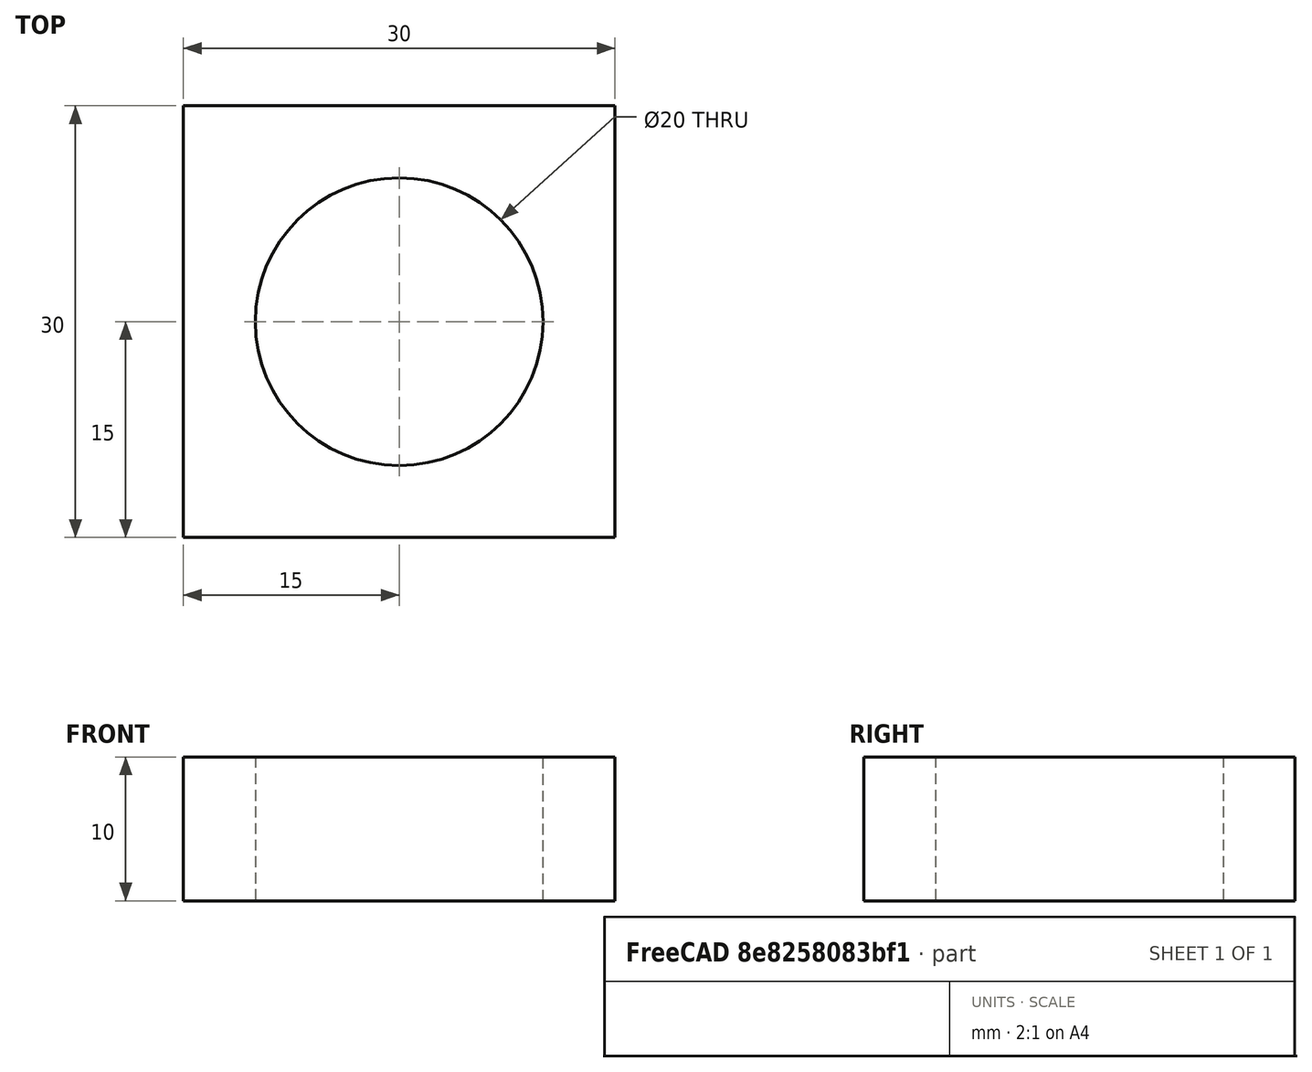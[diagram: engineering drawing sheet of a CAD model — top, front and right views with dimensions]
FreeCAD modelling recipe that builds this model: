
FCSTD DOCUMENT  (FreeCAD 0.20R29177 +426 (Git))
Label: SquareWasher
License: All rights reserved
LicenseURL: https://en.wikipedia.org/wiki/All_rights_reserved
objects: PartDesign::CoordinateSystem×2, Sketcher::SketchObject×1, PartDesign::Pad×1, PartDesign::Body×1, App::Part×1
note: 6 computed .brp shape members not serialized (recipe doc carries the construction recipe); baked Part::Feature solids carry a one-line shape summary decoded from their .brp

FEATURE [Sketcher::SketchObject] Sketch
  FullyConstrained = true
  MapMode = 5
  Support = -> [XY_Plane]
  sketch-geometry (5):
    g0: Circle CenterX=0 CenterY=0 CenterZ=0 NormalX=0 NormalY=0 NormalZ=1 AngleXU=0 Radius=10
    g1: LineSegment StartX=-15 StartY=15 StartZ=0 EndX=15 EndY=15 EndZ=0
    g2: LineSegment StartX=15 StartY=15 StartZ=0 EndX=15 EndY=-15 EndZ=0
    g3: LineSegment StartX=15 StartY=-15 StartZ=0 EndX=-15 EndY=-15 EndZ=0
    g4: LineSegment StartX=-15 StartY=-15 StartZ=0 EndX=-15 EndY=15 EndZ=0
  constraints (14):
    c: Coincident(g0,g-1)
    c: Diameter(g0) = 20
    c: Coincident(g1,g2)
    c: Coincident(g2,g3)
    c: Coincident(g3,g4)
    c: Coincident(g4,g1)
    c: Horizontal(g1)
    c: Horizontal(g3)
    c: Vertical(g2)
    c: Vertical(g4)
    c: Equal(g1,g4)
    c: DistanceY(g2,g2) = 30
    c: DistanceY(g3,g0) = 15
    c: DistanceX(g3,g0) = 15
FEATURE [PartDesign::Pad] Pad
  Direction = (0,0,1)
  Length = 10
  Length2 = 10
  Profile = -> Sketch
  ReferenceAxis = -> Sketch [N_Axis]
  Refine = true
  Type = 0
FEATURE [PartDesign::Body] Body  label="SquareWasherBody"
  Group = -> [Sketch,Pad]
  Origin = -> Origin
  Tip = -> Pad
FEATURE [PartDesign::CoordinateSystem] LCS_1
  AttacherType = Attacher::AttachEngine3D
  MapMode = 45
  Placement = pos=(7e-16,-3.2e-15,0) rot=(0,0,1;0rad)
  Support = -> [Pad]
FEATURE [PartDesign::CoordinateSystem] LCS_Spring
  AttacherType = Attacher::AttachEngine3D
  MapMode = 7
  Placement = pos=(10,0,10) rot=(1,0,0;1.5708rad)
  Support = -> [Pad]
FEATURE [App::Part] Part  label="SquareWasherPart"
  Group = -> [Body,LCS_1,LCS_Spring]
  Origin = -> Origin001
